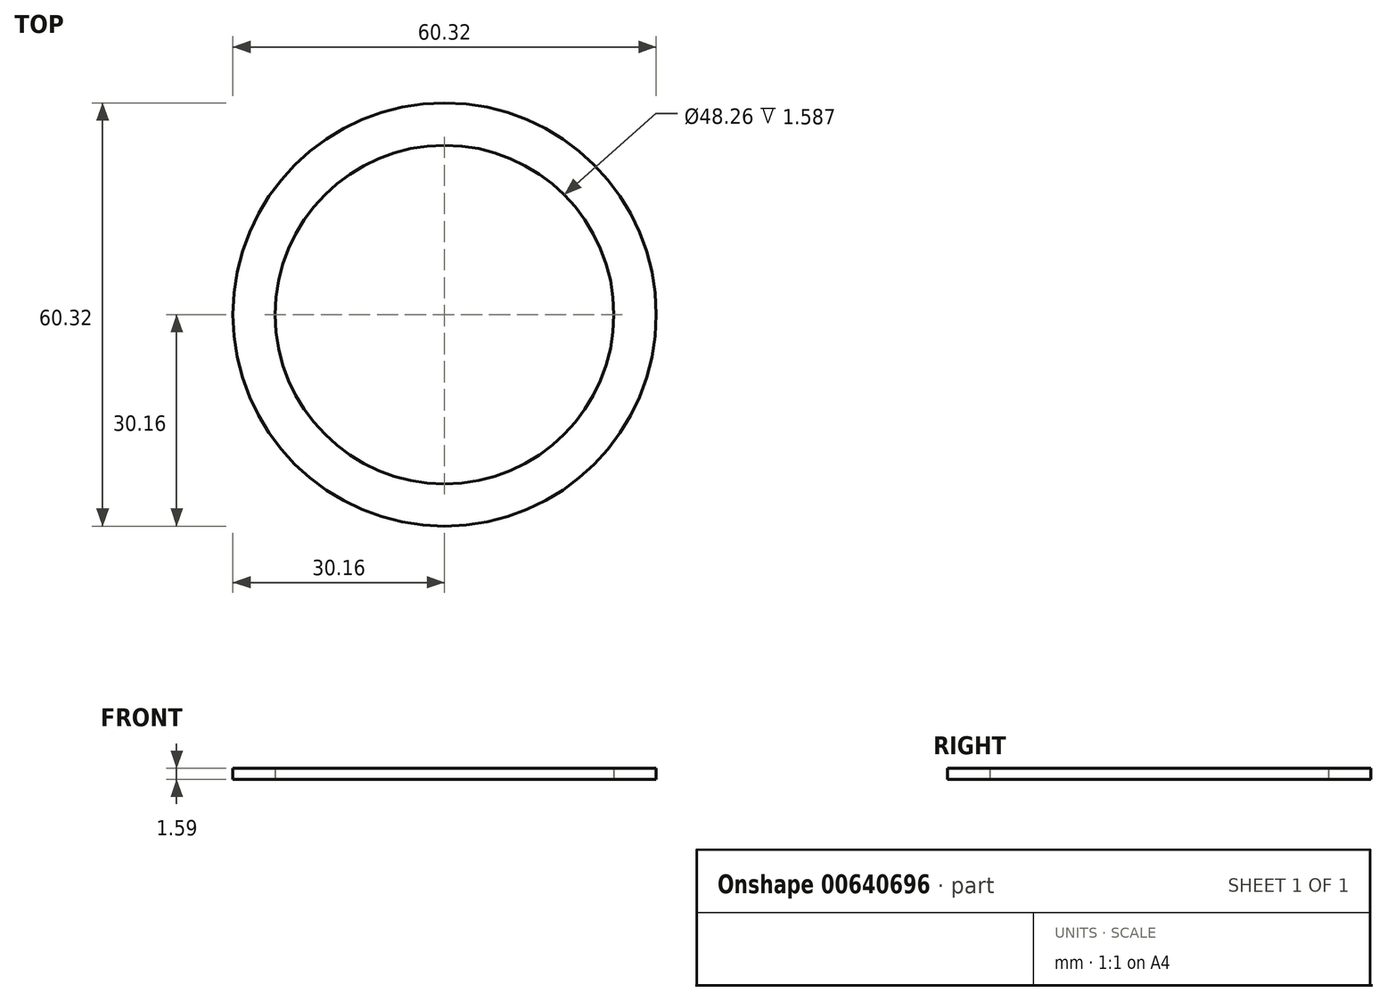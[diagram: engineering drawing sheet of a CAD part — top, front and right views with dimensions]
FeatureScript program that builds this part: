
annotation { "Feature Type Name" : "Feature", "Feature Type Description" : "" }
export const myFeature = defineFeature(function(context is Context, id is Id, definition is map)
    precondition{}
    {
        {
            var Q0;
            Q0=qCreatedBy(makeId("Top.planeOp"),FACE);
            var sketch = newSketch(context, id + "F0", { "sketchPlane" : qUnion([Q0])});
            skCircle(sketch, "E0", {"center": v(0, 0) * mm, "radius": 30.16 * mm});
            skCircle(sketch, "E1", {"center": v(0, 0) * mm, "radius": 24.13 * mm});
            skSolve(sketch);
        }
        {
            var Q0;
            Q0 = qSketchRegion(id + "F0", true);
            extrude(context, id + "F1", {"entities" : qUnion([Q0]), "depth" : 1.59 * mm, "offsetDistance" : 25.4 * mm});
        }
    });
